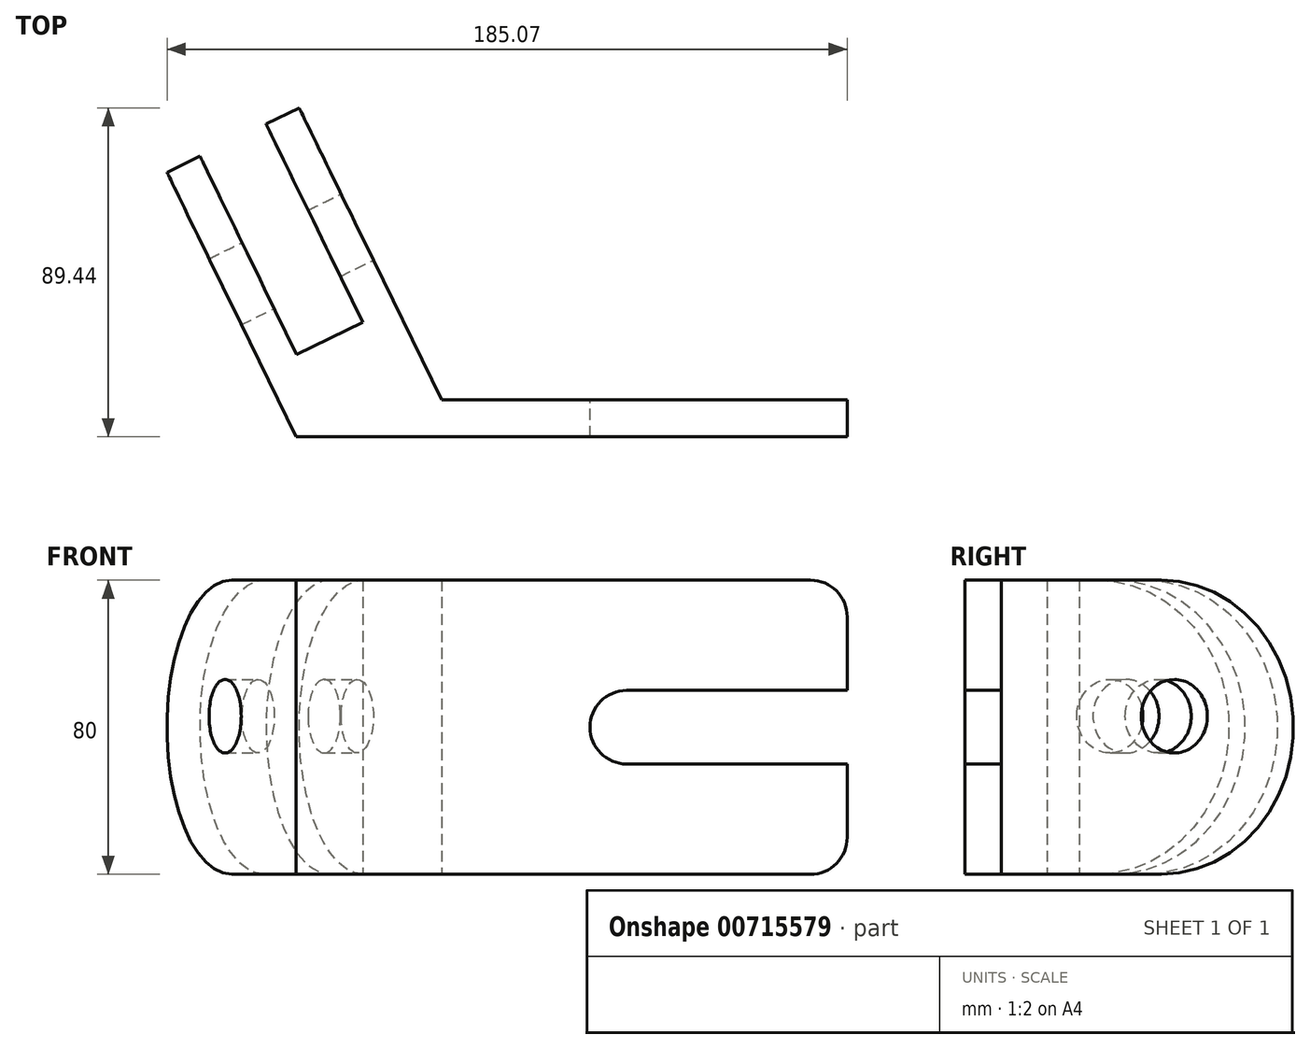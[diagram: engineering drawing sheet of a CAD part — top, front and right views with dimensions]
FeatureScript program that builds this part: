
annotation { "Feature Type Name" : "Feature", "Feature Type Description" : "" }
export const myFeature = defineFeature(function(context is Context, id is Id, definition is map)
    precondition{}
    {
        {
            var Q0;
            Q0=qCreatedBy(makeId("Top.planeOp"),FACE);
            var sketch = newSketch(context, id + "F0", { "sketchPlane" : qUnion([Q0])});
            skLineSegment(sketch, "E0", {"start": v(74.38, 0) * mm, "end": v(-75.62, 0) * mm});
            skLineSegment(sketch, "E1", {"start": v(-75.62, 0) * mm, "end": v(-110.7, 71.9) * mm});
            skLineSegment(sketch, "E2", {"start": v(-110.7, 71.9) * mm, "end": v(-101.7, 76.29) * mm});
            skLineSegment(sketch, "E3", {"start": v(74.38, 0) * mm, "end": v(74.38, 10) * mm});
            skLineSegment(sketch, "E4", {"start": v(-101.7, 76.29) * mm, "end": v(-75.4, 22.36) * mm});
            skLineSegment(sketch, "E5", {"start": v(-75.4, 22.36) * mm, "end": v(-57.43, 31.13) * mm});
            skLineSegment(sketch, "E6", {"start": v(-57.43, 31.13) * mm, "end": v(-83.73, 85.05) * mm});
            skLineSegment(sketch, "E7", {"start": v(-83.73, 85.05) * mm, "end": v(-74.74, 89.44) * mm});
            skLineSegment(sketch, "E8", {"start": v(74.38, 10) * mm, "end": v(-36, 10) * mm});
            skLineSegment(sketch, "E9", {"start": v(-74.74, 89.44) * mm, "end": v(-36, 10) * mm});
            skSolve(sketch);
        }
        {
            var Q0;
            Q0 = qSketchRegion(id + "F0", true);
            extrude(context, id + "F1", {"entities" : qUnion([Q0]), "depth" : 80 * mm, "offsetDistance" : 25 * mm});
        }
        {
            var Q0;
            Q0=makeQuery(id+"F1.opExtrude","SWEPT_FACE",FACE,{"disambiguationData":[OSD([sQuery(id+"F0.wireOp",EDGE,"E8")])]});
            var sketch = newSketch(context, id + "F2", { "sketchPlane" : qUnion([Q0])});
            skLineSegment(sketch, "E10.bottom", {"start": v(-14.38, 30) * mm, "end": v(-134.38, 30) * mm});
            skLineSegment(sketch, "E10.top", {"start": v(-14.38, 50) * mm, "end": v(-134.38, 50) * mm});
            skLineSegment(sketch, "E10.left", {"start": v(-14.38, 30) * mm, "end": v(-14.38, 50) * mm});
            skLineSegment(sketch, "E10.right", {"start": v(-134.38, 30) * mm, "end": v(-134.38, 50) * mm});
            skPoint(sketch, "E10.middle", {"position": v(-74.38, 40) * mm});
            skCircle(sketch, "E11", {"center": v(-14.38, 40) * mm, "radius": 10 * mm});
            skSolve(sketch);
        }
        {
            var Q0;
            Q0 = qSketchRegion(id + "F2", true);
            extrude(context, id + "F3", {"entities" : qUnion([Q0]), "operationType" : NewBodyOperationType.REMOVE, "oppositeDirection" : true, "depth" : 25 * mm, "offsetDistance" : 25 * mm});
        }
        {
            var Q0;
            Q0=makeQuery(id+"F1.opExtrude","CAP_EDGE",EDGE,{"disambiguationData":[OSD([sQuery(id+"F0.wireOp",EDGE,"E7")])],"isStart":false});
            var Q1;
            Q1=makeQuery(id+"F1.opExtrude","CAP_EDGE",EDGE,{"disambiguationData":[OSD([sQuery(id+"F0.wireOp",EDGE,"E2")])],"isStart":false});
            var Q2;
            Q2=makeQuery(id+"F1.opExtrude","CAP_EDGE",EDGE,{"disambiguationData":[OSD([sQuery(id+"F0.wireOp",EDGE,"E2")])],"isStart":true});
            var Q3;
            Q3=makeQuery(id+"F1.opExtrude","CAP_EDGE",EDGE,{"disambiguationData":[OSD([sQuery(id+"F0.wireOp",EDGE,"E7")])],"isStart":true});
            fillet(context, id + "F4", {"entities" : qUnion([Q0, Q1, Q2, Q3]), "radius" : 40 * mm, "tangentPropagation" : true, "allowEdgeOverflow" : false});
        }
        {
            var Q0;
            Q0=makeQuery(id+"F1.opExtrude","SWEPT_FACE",FACE,{"disambiguationData":[OSD([sQuery(id+"F0.wireOp",EDGE,"E9")])]});
            var sketch = newSketch(context, id + "F5", { "sketchPlane" : qUnion([Q0])});
            skSolve(sketch);
        }
        {
            var Q0;
            {var subQ0=sQuery(id+"F0.wireOp",EDGE,"E9");Q0=makeQuery(id+"F5.imprint","IMPRINT",FACE,{"disambiguationData":[TD([[makeQuery(id+"F5.imprint","IMPRINT",EDGE,{"derivedFrom":makeQuery(id+"F1.opExtrude","CAP_EDGE",EDGE,{"disambiguationData":[OSD([subQ0])],"isStart":true})}),-1.0]])]});}
            var sketch = newSketch(context, id + "F6", { "sketchPlane" : qUnion([Q0])});
            skCircle(sketch, "E12", {"center": v(77.07, 43) * mm, "radius": 10 * mm});
            skSolve(sketch);
        }
        {
            var Q0;
            Q0 = qSketchRegion(id + "F6", true);
            extrude(context, id + "F7", {"entities" : qUnion([Q0]), "operationType" : NewBodyOperationType.REMOVE, "oppositeDirection" : true, "depth" : 101.1 * mm, "offsetDistance" : 25 * mm});
        }
        {
            var Q0;
            Q0=makeQuery(id+"F1.opExtrude","CAP_EDGE",EDGE,{"disambiguationData":[OSD([sQuery(id+"F0.wireOp",EDGE,"E3")])],"isStart":false});
            var Q1;
            Q1=makeQuery(id+"F1.opExtrude","CAP_EDGE",EDGE,{"disambiguationData":[OSD([sQuery(id+"F0.wireOp",EDGE,"E3")])],"isStart":true});
            fillet(context, id + "F8", {"entities" : qUnion([Q0, Q1]), "radius" : 10 * mm, "tangentPropagation" : true, "allowEdgeOverflow" : false});
        }
    });
